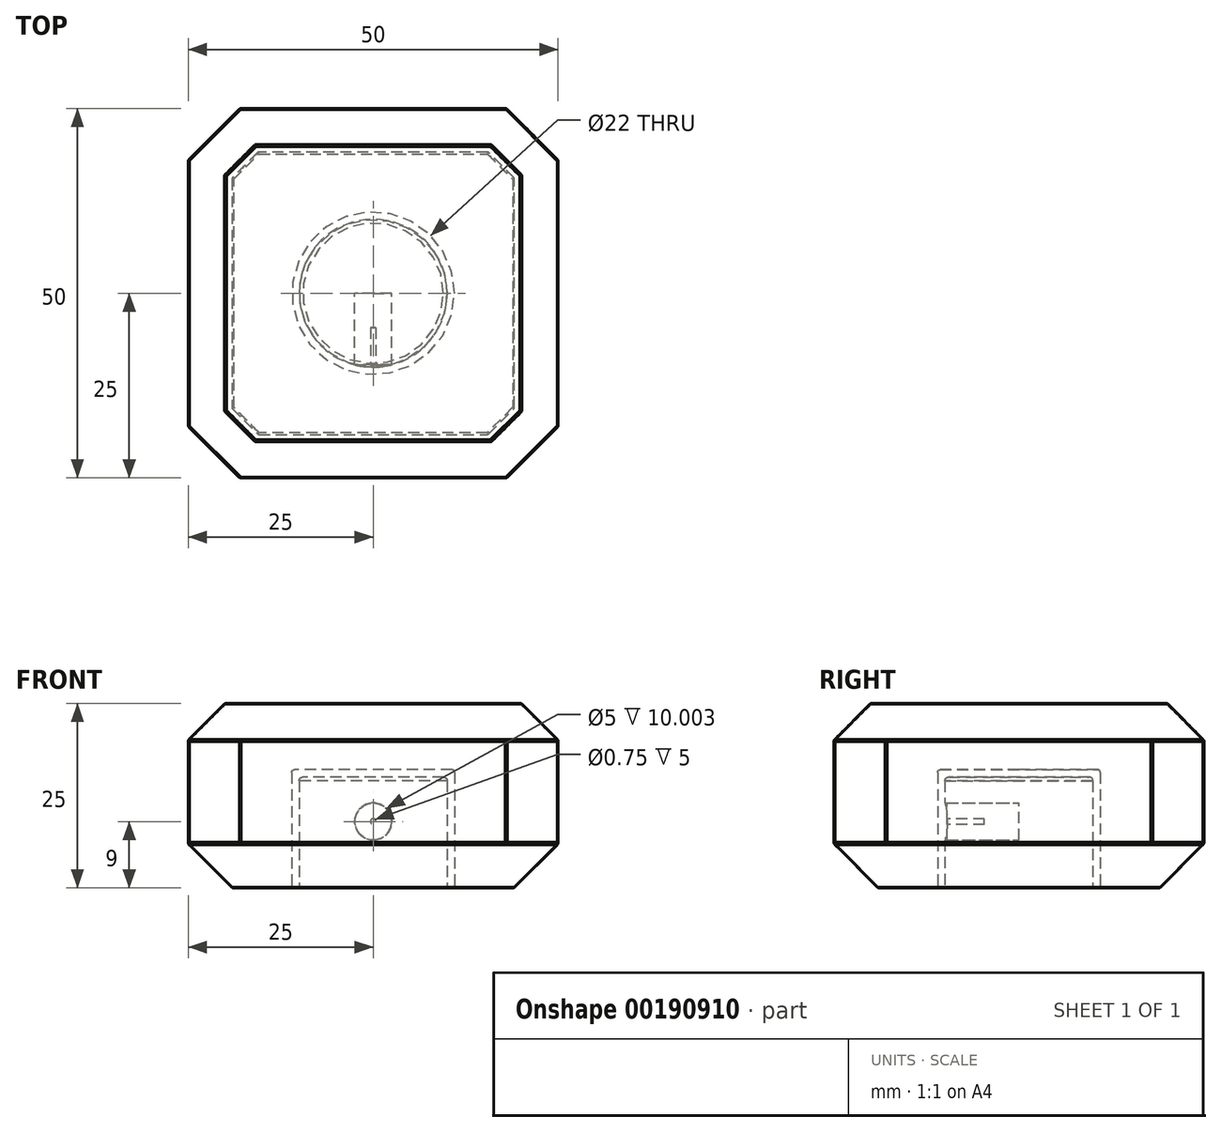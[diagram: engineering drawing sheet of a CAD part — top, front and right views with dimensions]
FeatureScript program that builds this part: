
annotation { "Feature Type Name" : "Feature", "Feature Type Description" : "" }
export const myFeature = defineFeature(function(context is Context, id is Id, definition is map)
    precondition{}
    {
        {
            var Q0;
            Q0=qCreatedBy(makeId("Top.planeOp"),FACE);
            var sketch = newSketch(context, id + "F0", { "sketchPlane" : qUnion([Q0])});
            skLineSegment(sketch, "E0.bottom", {"start": v(25, 25) * mm, "end": v(-25, 25) * mm});
            skLineSegment(sketch, "E0.top", {"start": v(25, -25) * mm, "end": v(-25, -25) * mm});
            skLineSegment(sketch, "E0.left", {"start": v(25, 25) * mm, "end": v(25, -25) * mm});
            skLineSegment(sketch, "E0.right", {"start": v(-25, 25) * mm, "end": v(-25, -25) * mm});
            skPoint(sketch, "E0.middle", {"position": v(0, 0) * mm});
            skSolve(sketch);
        }
        {
            var Q0;
            Q0 = qSketchRegion(id + "F0", true);
            extrude(context, id + "F1", {"entities" : qUnion([Q0]), "depth" : 25 * mm, "offsetDistance" : 25 * mm});
        }
        {
            var Q0;
            Q0=qCreatedBy(makeId("Top.planeOp"),FACE);
            var sketch = newSketch(context, id + "F2", { "sketchPlane" : qUnion([Q0])});
            skCircle(sketch, "E1", {"center": v(0, 0) * mm, "radius": 10 * mm});
            skSolve(sketch);
        }
        {
            var Q0;
            Q0 = qSketchRegion(id + "F2", true);
            extrude(context, id + "F3", {"entities" : qUnion([Q0]), "depth" : 15 * mm, "offsetDistance" : 25 * mm});
        }
        {
            var Q0;
            Q0=makeQuery(id+"F3.opExtrude","SWEPT_BODY",BODY,{"disambiguationData":[OSD([sQuery(id+"F2.wireOp",EDGE,"E1")])]});
            var Q1;
            Q1=makeQuery(id+"F1.opExtrude","SWEPT_BODY",BODY,{"disambiguationData":[OSD([sQuery(id+"F0.wireOp",EDGE,"E0.bottom"),sQuery(id+"F0.wireOp",EDGE,"E0.top"),sQuery(id+"F0.wireOp",EDGE,"E0.left"),sQuery(id+"F0.wireOp",EDGE,"E0.right")])]});
            booleanBodies(context, id + "F4", {"operationType" : BooleanOperationType.SUBTRACTION, "tools" : qUnion([Q0]), "targets" : qUnion([Q1]), "offset" : true, "offsetAll" : true, "offsetDistance" : 1 * mm, "keepTools" : true});
        }
        {
            var Q0;
            Q0=makeQuery(id+"F3.opExtrude","CAP_FACE",FACE,{"disambiguationData":[OSD([sQuery(id+"F2.wireOp",EDGE,"E1")])],"isStart":false});
            var sketch = newSketch(context, id + "F5", { "sketchPlane" : qUnion([Q0])});
            skLineSegment(sketch, "E2", {"start": v(-2.5, -9.68) * mm, "end": v(2.5, -9.68) * mm, "construction": true});
            skLineSegment(sketch, "E3", {"start": v(0, -9.68) * mm, "end": v(0, 0) * mm, "construction": true});
            skSolve(sketch);
        }
        {
            var Q0;
            Q0=qCreatedBy(makeId("Front.planeOp"),FACE);
            var sketch = newSketch(context, id + "F6", { "sketchPlane" : qUnion([Q0])});
            skCircle(sketch, "E4", {"center": v(0, 9) * mm, "radius": 2.5 * mm});
            skSolve(sketch);
        }
        {
            var Q0;
            Q0 = qSketchRegion(id + "F6", true);
            extrude(context, id + "F7", {"entities" : qUnion([Q0]), "operationType" : NewBodyOperationType.REMOVE, "endBound" : BoundingType.UP_TO_NEXT, "depth" : 25 * mm, "offsetDistance" : 25 * mm});
        }
        {
            var Q0;
            Q0=makeQuery(id+"F7.boolean.opBoolean","COPY",FACE,{"derivedFrom":makeQuery(id+"F7.opExtrude","CAP_FACE",FACE,{"disambiguationData":[OSD([sQuery(id+"F6.wireOp",EDGE,"E4")])],"isStart":true})});
            var Q1;
            Q1=sQuery(id+"F5.wireOp",VERTEX,"E3.start");
            extrude(context, id + "F8", {"entities" : qUnion([Q0]), "endBound" : BoundingType.UP_TO_VERTEX, "depth" : 25 * mm, "endBoundEntityVertex" : qUnion([Q1]), "offsetDistance" : 25 * mm});
        }
        {
            var Q0;
            Q0=makeQuery(id+"F8.opExtrude","CAP_FACE",FACE,{"disambiguationData":[OSD([sQuery(id+"F6.wireOp",EDGE,"E4")])],"isStart":false});
            var sketch = newSketch(context, id + "F9", { "sketchPlane" : qUnion([Q0])});
            skCircle(sketch, "E5", {"center": v(0, 9) * mm, "radius": 0.38 * mm});
            skSolve(sketch);
        }
        {
            var Q0;
            Q0 = qSketchRegion(id + "F9", true);
            extrude(context, id + "F10", {"entities" : qUnion([Q0]), "operationType" : NewBodyOperationType.REMOVE, "oppositeDirection" : true, "depth" : 5 * mm, "offsetDistance" : 25 * mm});
        }
        {
            var Q0;
            Q0=makeQuery(id+"F3.opExtrude","CAP_FACE",FACE,{"disambiguationData":[OSD([sQuery(id+"F2.wireOp",EDGE,"E1")])],"isStart":false});
            fillet(context, id + "F11", {"entities" : qUnion([Q0]), "tangentPropagation" : true, "crossSection" : FilletCrossSection.CURVATURE, "radius" : 0.5 * mm, "magnitude" : 0.5, "defaultsChanged" : true, "vertexSettings" : []});
        }
        {
            var Q0;
            Q0=makeQuery(id+"F1.opExtrude","SWEPT_EDGE",EDGE,{"disambiguationData":[OSD([sQuery(id+"F0.wireOp",EDGE,"E0.top"),sQuery(id+"F0.wireOp",EDGE,"E0.left")])]});
            var Q1;
            Q1=makeQuery(id+"F1.opExtrude","SWEPT_EDGE",EDGE,{"disambiguationData":[OSD([sQuery(id+"F0.wireOp",EDGE,"E0.bottom"),sQuery(id+"F0.wireOp",EDGE,"E0.left")])]});
            var Q2;
            Q2=makeQuery(id+"F1.opExtrude","SWEPT_EDGE",EDGE,{"disambiguationData":[OSD([sQuery(id+"F0.wireOp",EDGE,"E0.bottom"),sQuery(id+"F0.wireOp",EDGE,"E0.right")])]});
            var Q3;
            Q3=makeQuery(id+"F1.opExtrude","SWEPT_EDGE",EDGE,{"disambiguationData":[OSD([sQuery(id+"F0.wireOp",EDGE,"E0.top"),sQuery(id+"F0.wireOp",EDGE,"E0.right")])]});
            chamfer(context, id + "F12", {"entities" : qUnion([Q0, Q1, Q2, Q3]), "width" : 7 * mm, "tangentPropagation" : true});
        }
        {
            var Q0;
            Q0=makeQuery(id+"F1.opExtrude","CAP_FACE",FACE,{"disambiguationData":[OSD([sQuery(id+"F0.wireOp",EDGE,"E0.bottom"),sQuery(id+"F0.wireOp",EDGE,"E0.top"),sQuery(id+"F0.wireOp",EDGE,"E0.left"),sQuery(id+"F0.wireOp",EDGE,"E0.right")])],"isStart":false});
            chamfer(context, id + "F13", {"entities" : qUnion([Q0]), "width" : 5 * mm, "tangentPropagation" : true});
        }
        {
            var Q0;
            {var subQ0=sQuery(id+"F0.wireOp",EDGE,"E0.right");var subQ1=sQuery(id+"F0.wireOp",EDGE,"E0.top");Q0=makeQuery(id+"F12.opChamfer","BLEND_EDGE",EDGE,{"blendedFrom":[makeQuery(id+"F1.opExtrude","SWEPT_EDGE",EDGE,{"disambiguationData":[OSD([subQ1,subQ0])]}),makeQuery(id+"F1.opExtrude","CAP_FACE",FACE,{"disambiguationData":[OSD([sQuery(id+"F0.wireOp",EDGE,"E0.bottom"),subQ1,sQuery(id+"F0.wireOp",EDGE,"E0.left"),subQ0])],"isStart":true})],"blendedInto":[makeQuery(id+"F1.opExtrude","CAP_FACE",FACE,{"disambiguationData":[OSD([sQuery(id+"F0.wireOp",EDGE,"E0.bottom"),subQ1,sQuery(id+"F0.wireOp",EDGE,"E0.left"),subQ0])],"isStart":true})]});}
            var Q1;
            Q1=makeQuery(id+"F1.opExtrude","CAP_EDGE",EDGE,{"disambiguationData":[OSD([sQuery(id+"F0.wireOp",EDGE,"E0.right")])],"isStart":true});
            var Q2;
            {var subQ0=sQuery(id+"F0.wireOp",EDGE,"E0.right");var subQ1=sQuery(id+"F0.wireOp",EDGE,"E0.bottom");Q2=makeQuery(id+"F12.opChamfer","BLEND_EDGE",EDGE,{"blendedFrom":[makeQuery(id+"F1.opExtrude","SWEPT_EDGE",EDGE,{"disambiguationData":[OSD([subQ1,subQ0])]}),makeQuery(id+"F1.opExtrude","CAP_FACE",FACE,{"disambiguationData":[OSD([subQ1,sQuery(id+"F0.wireOp",EDGE,"E0.top"),sQuery(id+"F0.wireOp",EDGE,"E0.left"),subQ0])],"isStart":true})],"blendedInto":[makeQuery(id+"F1.opExtrude","CAP_FACE",FACE,{"disambiguationData":[OSD([subQ1,sQuery(id+"F0.wireOp",EDGE,"E0.top"),sQuery(id+"F0.wireOp",EDGE,"E0.left"),subQ0])],"isStart":true})]});}
            var Q3;
            Q3=makeQuery(id+"F1.opExtrude","CAP_EDGE",EDGE,{"disambiguationData":[OSD([sQuery(id+"F0.wireOp",EDGE,"E0.bottom")])],"isStart":true});
            var Q4;
            {var subQ0=sQuery(id+"F0.wireOp",EDGE,"E0.left");var subQ1=sQuery(id+"F0.wireOp",EDGE,"E0.bottom");Q4=makeQuery(id+"F12.opChamfer","BLEND_EDGE",EDGE,{"blendedFrom":[makeQuery(id+"F1.opExtrude","SWEPT_EDGE",EDGE,{"disambiguationData":[OSD([subQ1,subQ0])]}),makeQuery(id+"F1.opExtrude","CAP_FACE",FACE,{"disambiguationData":[OSD([subQ1,sQuery(id+"F0.wireOp",EDGE,"E0.top"),subQ0,sQuery(id+"F0.wireOp",EDGE,"E0.right")])],"isStart":true})],"blendedInto":[makeQuery(id+"F1.opExtrude","CAP_FACE",FACE,{"disambiguationData":[OSD([subQ1,sQuery(id+"F0.wireOp",EDGE,"E0.top"),subQ0,sQuery(id+"F0.wireOp",EDGE,"E0.right")])],"isStart":true})]});}
            var Q5;
            Q5=makeQuery(id+"F1.opExtrude","CAP_EDGE",EDGE,{"disambiguationData":[OSD([sQuery(id+"F0.wireOp",EDGE,"E0.left")])],"isStart":true});
            var Q6;
            {var subQ0=sQuery(id+"F0.wireOp",EDGE,"E0.left");var subQ1=sQuery(id+"F0.wireOp",EDGE,"E0.top");Q6=makeQuery(id+"F12.opChamfer","BLEND_EDGE",EDGE,{"blendedFrom":[makeQuery(id+"F1.opExtrude","SWEPT_EDGE",EDGE,{"disambiguationData":[OSD([subQ1,subQ0])]}),makeQuery(id+"F1.opExtrude","CAP_FACE",FACE,{"disambiguationData":[OSD([sQuery(id+"F0.wireOp",EDGE,"E0.bottom"),subQ1,subQ0,sQuery(id+"F0.wireOp",EDGE,"E0.right")])],"isStart":true})],"blendedInto":[makeQuery(id+"F1.opExtrude","CAP_FACE",FACE,{"disambiguationData":[OSD([sQuery(id+"F0.wireOp",EDGE,"E0.bottom"),subQ1,subQ0,sQuery(id+"F0.wireOp",EDGE,"E0.right")])],"isStart":true})]});}
            var Q7;
            Q7=makeQuery(id+"F1.opExtrude","CAP_EDGE",EDGE,{"disambiguationData":[OSD([sQuery(id+"F0.wireOp",EDGE,"E0.top")])],"isStart":true});
            chamfer(context, id + "F14", {"entities" : qUnion([Q0, Q1, Q2, Q3, Q4, Q5, Q6, Q7]), "width" : 6 * mm, "tangentPropagation" : true});
        }
        {
            var Q0;
            Q0=makeQuery(id+"F1.opExtrude","CAP_FACE",FACE,{"disambiguationData":[OSD([sQuery(id+"F0.wireOp",EDGE,"E0.bottom"),sQuery(id+"F0.wireOp",EDGE,"E0.top"),sQuery(id+"F0.wireOp",EDGE,"E0.left"),sQuery(id+"F0.wireOp",EDGE,"E0.right")])],"isStart":false});
            var Q1;
            Q1=makeQuery(id+"F1.opExtrude","SWEPT_FACE",FACE,{"disambiguationData":[OSD([sQuery(id+"F0.wireOp",EDGE,"E0.top")])]});
            var Q2;
            Q2=makeQuery(id+"F1.opExtrude","SWEPT_FACE",FACE,{"disambiguationData":[OSD([sQuery(id+"F0.wireOp",EDGE,"E0.left")])]});
            var Q3;
            {var subQ0=sQuery(id+"F0.wireOp",EDGE,"E0.right");var subQ1=sQuery(id+"F0.wireOp",EDGE,"E0.left");var subQ2=sQuery(id+"F0.wireOp",EDGE,"E0.top");var subQ3=sQuery(id+"F0.wireOp",EDGE,"E0.bottom");Q3=makeQuery(id+"F13.opChamfer","BLEND_FACE",FACE,{"disambiguationData":[OSD([subQ3,subQ2,subQ1,subQ0]),TDD([makeQuery(id+"F12.opChamfer","BLEND_EDGE",EDGE,{"blendedFrom":[makeQuery(id+"F1.opExtrude","SWEPT_EDGE",EDGE,{"disambiguationData":[OSD([subQ2,subQ1])]}),makeQuery(id+"F1.opExtrude","CAP_FACE",FACE,{"disambiguationData":[OSD([subQ3,subQ2,subQ1,subQ0])],"isStart":false})],"blendedInto":[makeQuery(id+"F1.opExtrude","CAP_FACE",FACE,{"disambiguationData":[OSD([subQ3,subQ2,subQ1,subQ0])],"isStart":false})]})])]});}
            var Q4;
            {var subQ0=sQuery(id+"F0.wireOp",EDGE,"E0.right");var subQ1=sQuery(id+"F0.wireOp",EDGE,"E0.left");var subQ2=sQuery(id+"F0.wireOp",EDGE,"E0.top");var subQ3=sQuery(id+"F0.wireOp",EDGE,"E0.bottom");Q4=makeQuery(id+"F13.opChamfer","BLEND_FACE",FACE,{"disambiguationData":[OSD([subQ3,subQ2,subQ1,subQ0]),TDD([makeQuery(id+"F12.opChamfer","BLEND_EDGE",EDGE,{"blendedFrom":[makeQuery(id+"F1.opExtrude","SWEPT_EDGE",EDGE,{"disambiguationData":[OSD([subQ2,subQ0])]}),makeQuery(id+"F1.opExtrude","CAP_FACE",FACE,{"disambiguationData":[OSD([subQ3,subQ2,subQ1,subQ0])],"isStart":false})],"blendedInto":[makeQuery(id+"F1.opExtrude","CAP_FACE",FACE,{"disambiguationData":[OSD([subQ3,subQ2,subQ1,subQ0])],"isStart":false})]})])]});}
            var Q5;
            Q5=makeQuery(id+"F1.opExtrude","SWEPT_FACE",FACE,{"disambiguationData":[OSD([sQuery(id+"F0.wireOp",EDGE,"E0.right")])]});
            var Q6;
            {var subQ0=sQuery(id+"F0.wireOp",EDGE,"E0.right");var subQ1=sQuery(id+"F0.wireOp",EDGE,"E0.left");var subQ2=sQuery(id+"F0.wireOp",EDGE,"E0.top");var subQ3=sQuery(id+"F0.wireOp",EDGE,"E0.bottom");Q6=makeQuery(id+"F13.opChamfer","BLEND_FACE",FACE,{"disambiguationData":[OSD([subQ3,subQ2,subQ1,subQ0]),TDD([makeQuery(id+"F12.opChamfer","BLEND_EDGE",EDGE,{"blendedFrom":[makeQuery(id+"F1.opExtrude","SWEPT_EDGE",EDGE,{"disambiguationData":[OSD([subQ3,subQ0])]}),makeQuery(id+"F1.opExtrude","CAP_FACE",FACE,{"disambiguationData":[OSD([subQ3,subQ2,subQ1,subQ0])],"isStart":false})],"blendedInto":[makeQuery(id+"F1.opExtrude","CAP_FACE",FACE,{"disambiguationData":[OSD([subQ3,subQ2,subQ1,subQ0])],"isStart":false})]})])]});}
            var Q7;
            Q7=makeQuery(id+"F1.opExtrude","SWEPT_FACE",FACE,{"disambiguationData":[OSD([sQuery(id+"F0.wireOp",EDGE,"E0.bottom")])]});
            var Q8;
            {var subQ0=sQuery(id+"F0.wireOp",EDGE,"E0.right");var subQ1=sQuery(id+"F0.wireOp",EDGE,"E0.left");var subQ2=sQuery(id+"F0.wireOp",EDGE,"E0.top");var subQ3=sQuery(id+"F0.wireOp",EDGE,"E0.bottom");Q8=makeQuery(id+"F13.opChamfer","BLEND_FACE",FACE,{"disambiguationData":[OSD([subQ3,subQ2,subQ1,subQ0]),TDD([makeQuery(id+"F12.opChamfer","BLEND_EDGE",EDGE,{"blendedFrom":[makeQuery(id+"F1.opExtrude","SWEPT_EDGE",EDGE,{"disambiguationData":[OSD([subQ3,subQ1])]}),makeQuery(id+"F1.opExtrude","CAP_FACE",FACE,{"disambiguationData":[OSD([subQ3,subQ2,subQ1,subQ0])],"isStart":false})],"blendedInto":[makeQuery(id+"F1.opExtrude","CAP_FACE",FACE,{"disambiguationData":[OSD([subQ3,subQ2,subQ1,subQ0])],"isStart":false})]})])]});}
            var Q9;
            {var subQ0=sQuery(id+"F0.wireOp",EDGE,"E0.right");var subQ1=sQuery(id+"F0.wireOp",EDGE,"E0.left");var subQ2=sQuery(id+"F0.wireOp",EDGE,"E0.top");var subQ3=sQuery(id+"F0.wireOp",EDGE,"E0.bottom");Q9=makeQuery(id+"F14.opChamfer","BLEND_FACE",FACE,{"disambiguationData":[OSD([subQ3,subQ2,subQ1,subQ0]),TDD([makeQuery(id+"F12.opChamfer","BLEND_EDGE",EDGE,{"blendedFrom":[makeQuery(id+"F1.opExtrude","SWEPT_EDGE",EDGE,{"disambiguationData":[OSD([subQ2,subQ1])]}),makeQuery(id+"F1.opExtrude","CAP_FACE",FACE,{"disambiguationData":[OSD([subQ3,subQ2,subQ1,subQ0])],"isStart":true})],"blendedInto":[makeQuery(id+"F1.opExtrude","CAP_FACE",FACE,{"disambiguationData":[OSD([subQ3,subQ2,subQ1,subQ0])],"isStart":true})]})])]});}
            var Q10;
            {var subQ0=sQuery(id+"F0.wireOp",EDGE,"E0.right");var subQ1=sQuery(id+"F0.wireOp",EDGE,"E0.left");var subQ2=sQuery(id+"F0.wireOp",EDGE,"E0.top");var subQ3=sQuery(id+"F0.wireOp",EDGE,"E0.bottom");Q10=makeQuery(id+"F14.opChamfer","BLEND_FACE",FACE,{"disambiguationData":[OSD([subQ3,subQ2,subQ1,subQ0]),TDD([makeQuery(id+"F12.opChamfer","BLEND_EDGE",EDGE,{"blendedFrom":[makeQuery(id+"F1.opExtrude","SWEPT_EDGE",EDGE,{"disambiguationData":[OSD([subQ3,subQ1])]}),makeQuery(id+"F1.opExtrude","CAP_FACE",FACE,{"disambiguationData":[OSD([subQ3,subQ2,subQ1,subQ0])],"isStart":true})],"blendedInto":[makeQuery(id+"F1.opExtrude","CAP_FACE",FACE,{"disambiguationData":[OSD([subQ3,subQ2,subQ1,subQ0])],"isStart":true})]})])]});}
            var Q11;
            {var subQ0=sQuery(id+"F0.wireOp",EDGE,"E0.right");var subQ1=sQuery(id+"F0.wireOp",EDGE,"E0.left");var subQ2=sQuery(id+"F0.wireOp",EDGE,"E0.top");var subQ3=sQuery(id+"F0.wireOp",EDGE,"E0.bottom");Q11=makeQuery(id+"F14.opChamfer","BLEND_FACE",FACE,{"disambiguationData":[OSD([subQ3,subQ2,subQ1,subQ0]),TDD([makeQuery(id+"F12.opChamfer","BLEND_EDGE",EDGE,{"blendedFrom":[makeQuery(id+"F1.opExtrude","SWEPT_EDGE",EDGE,{"disambiguationData":[OSD([subQ3,subQ0])]}),makeQuery(id+"F1.opExtrude","CAP_FACE",FACE,{"disambiguationData":[OSD([subQ3,subQ2,subQ1,subQ0])],"isStart":true})],"blendedInto":[makeQuery(id+"F1.opExtrude","CAP_FACE",FACE,{"disambiguationData":[OSD([subQ3,subQ2,subQ1,subQ0])],"isStart":true})]})])]});}
            var Q12;
            {var subQ0=sQuery(id+"F0.wireOp",EDGE,"E0.right");var subQ1=sQuery(id+"F0.wireOp",EDGE,"E0.left");var subQ2=sQuery(id+"F0.wireOp",EDGE,"E0.top");var subQ3=sQuery(id+"F0.wireOp",EDGE,"E0.bottom");Q12=makeQuery(id+"F14.opChamfer","BLEND_FACE",FACE,{"disambiguationData":[OSD([subQ3,subQ2,subQ1,subQ0]),TDD([makeQuery(id+"F12.opChamfer","BLEND_EDGE",EDGE,{"blendedFrom":[makeQuery(id+"F1.opExtrude","SWEPT_EDGE",EDGE,{"disambiguationData":[OSD([subQ2,subQ0])]}),makeQuery(id+"F1.opExtrude","CAP_FACE",FACE,{"disambiguationData":[OSD([subQ3,subQ2,subQ1,subQ0])],"isStart":true})],"blendedInto":[makeQuery(id+"F1.opExtrude","CAP_FACE",FACE,{"disambiguationData":[OSD([subQ3,subQ2,subQ1,subQ0])],"isStart":true})]})])]});}
            var Q13;
            Q13=makeQuery(id+"F1.opExtrude","CAP_FACE",FACE,{"disambiguationData":[OSD([sQuery(id+"F0.wireOp",EDGE,"E0.bottom"),sQuery(id+"F0.wireOp",EDGE,"E0.top"),sQuery(id+"F0.wireOp",EDGE,"E0.left"),sQuery(id+"F0.wireOp",EDGE,"E0.right")])],"isStart":true});
            var Q14;
            Q14=makeQuery(id+"F4.tempBoolean.opBoolean","COPY",FACE,{"derivedFrom":makeQuery(id+"F4.offsetTempBody.opPattern","COPY",FACE,{"derivedFrom":makeQuery(id+"F3.opExtrude","CAP_FACE",FACE,{"disambiguationData":[OSD([sQuery(id+"F2.wireOp",EDGE,"E1")])],"isStart":false}),"instanceName":"1"})});
            fillet(context, id + "F15", {"entities" : qUnion([Q0, Q1, Q2, Q3, Q4, Q5, Q6, Q7, Q8, Q9, Q10, Q11, Q12, Q13, Q14]), "tangentPropagation" : true, "crossSection" : FilletCrossSection.CURVATURE, "radius" : 0.35 * mm, "magnitude" : 0.5, "defaultsChanged" : true, "vertexSettings" : []});
        }
    });
